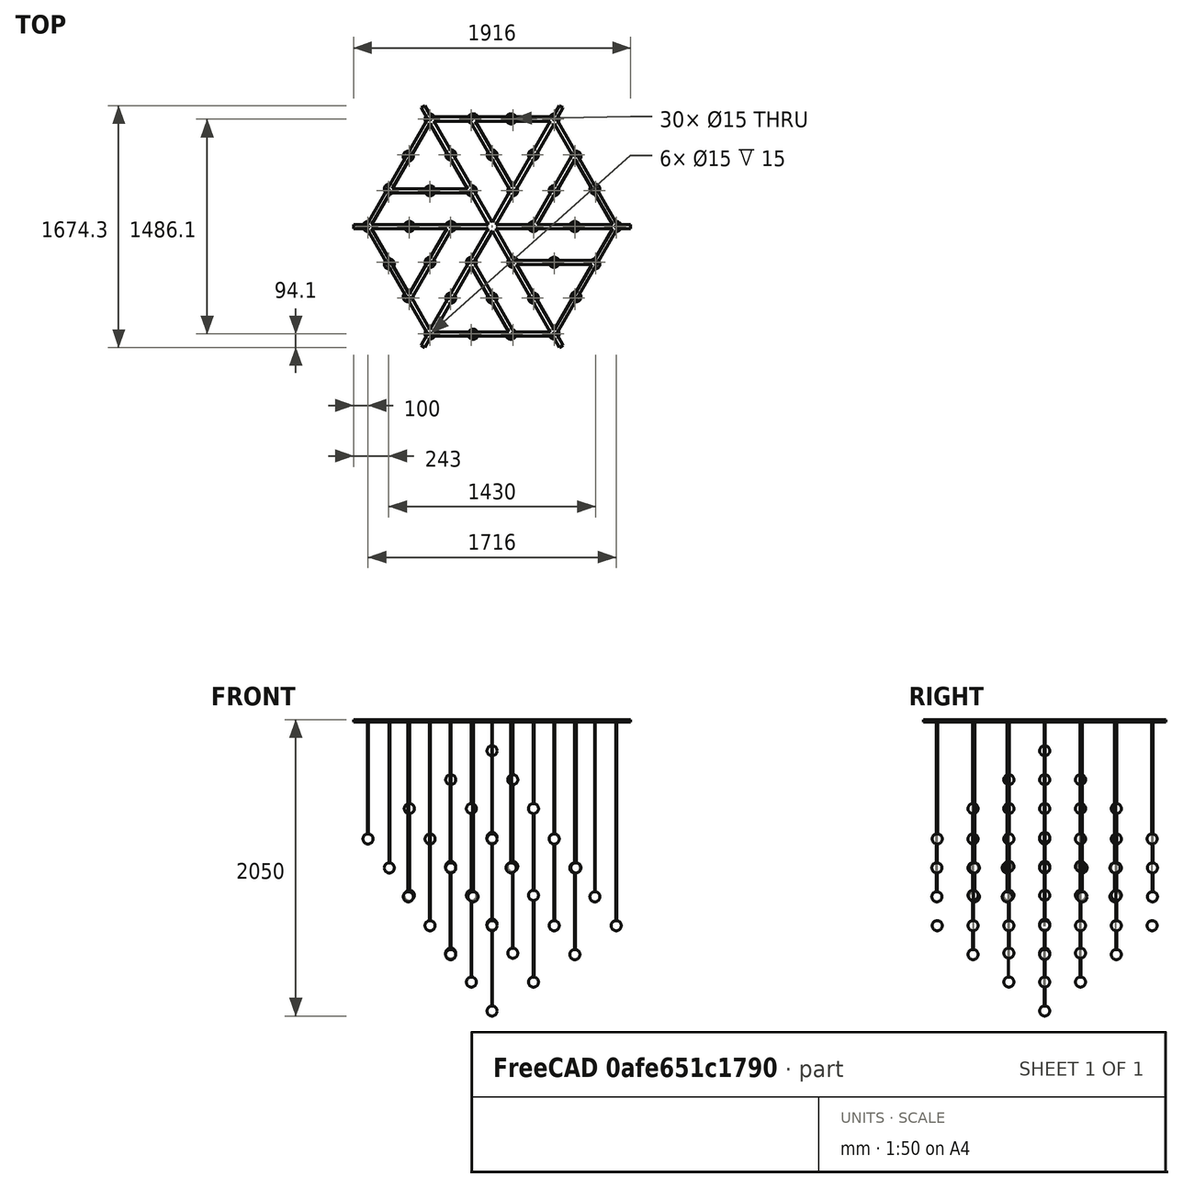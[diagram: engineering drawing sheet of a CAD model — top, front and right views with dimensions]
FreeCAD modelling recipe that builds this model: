
FCSTD DOCUMENT  (FreeCAD 0.19R)
Label: Doc_fabrication
License: Creative Commons Attribution-NonCommercial
LicenseURL: http://creativecommons.org/licenses/by-nc/4.0/
objects: Part::Sphere×64, Part::Fuse×49, Part::Cylinder×37, TechDraw::DrawViewDimension×27, Part::MultiFuse×23, Part::Box×18, TechDraw::DrawSVGTemplate×2, TechDraw::DrawViewPart×2, TechDraw::DrawPage×2, App::DocumentObjectGroup×2, PartDesign::FeatureBase×1, Sketcher::SketchObject×1, PartDesign::Pocket×1, PartDesign::PolarPattern×1, PartDesign::Body×1
note: 197 computed .brp shape members not serialized (recipe doc carries the construction recipe); baked Part::Feature solids carry a one-line shape summary decoded from their .brp

FEATURE [TechDraw::DrawSVGTemplate] Template
  Height = 210
  Orientation = 1
  Width = 297
FEATURE [Part::Cylinder] cylinder
  Angle = 360
  AttacherType = Attacher::AttachEngine3D
  Height = 2000
  Placement = pos=(0,0,-2000) rot=(0,0,1;0rad)
  Radius = 3
FEATURE [Part::Sphere] sphere
  Angle1 = -90
  Angle2 = 90
  Angle3 = 360
  AttacherType = Attacher::AttachEngine3D
  Placement = pos=(0,0,-200) rot=(0,0,1;0rad)
  Radius = 35
FEATURE [Part::Sphere] sphere001
  Angle1 = -90
  Angle2 = 90
  Angle3 = 360
  AttacherType = Attacher::AttachEngine3D
  Placement = pos=(0,0,-800) rot=(0,0,1;0rad)
  Radius = 35
FEATURE [Part::Sphere] sphere002
  Angle1 = -90
  Angle2 = 90
  Angle3 = 360
  AttacherType = Attacher::AttachEngine3D
  Placement = pos=(0,0,-1400) rot=(0,0,1;0rad)
  Radius = 35
FEATURE [Part::Sphere] sphere003
  Angle1 = -90
  Angle2 = 90
  Angle3 = 360
  AttacherType = Attacher::AttachEngine3D
  Placement = pos=(0,0,-2000) rot=(0,0,1;0rad)
  Radius = 35
FEATURE [Part::MultiFuse] Group
  Shapes = -> [sphere,sphere001,sphere002,sphere003]
FEATURE [Part::Fuse] Group001
  Base = -> cylinder
  Tool = -> Group
FEATURE [Part::Cylinder] cylinder001
  Angle = 360
  AttacherType = Attacher::AttachEngine3D
  Height = 1800
  Placement = pos=(0,0,-1800) rot=(0,0,1;0rad)
  Radius = 3
FEATURE [Part::Sphere] sphere004
  Angle1 = -90
  Angle2 = 90
  Angle3 = 360
  AttacherType = Attacher::AttachEngine3D
  Placement = pos=(0,0,-600) rot=(0,0,1;0rad)
  Radius = 35
FEATURE [Part::Sphere] sphere005
  Angle1 = -90
  Angle2 = 90
  Angle3 = 360
  AttacherType = Attacher::AttachEngine3D
  Placement = pos=(0,0,-1200) rot=(0,0,1;0rad)
  Radius = 35
FEATURE [Part::Sphere] sphere006
  Angle1 = -90
  Angle2 = 90
  Angle3 = 360
  AttacherType = Attacher::AttachEngine3D
  Placement = pos=(0,0,-1800) rot=(0,0,1;0rad)
  Radius = 35
FEATURE [Part::MultiFuse] Group002
  Shapes = -> [sphere004,sphere005,sphere006]
FEATURE [Part::Fuse] Group003
  Base = -> cylinder001
  Placement = pos=(286,0,0) rot=(0,0,1;0rad)
  Tool = -> Group002
FEATURE [Part::Cylinder] cylinder002
  Angle = 360
  AttacherType = Attacher::AttachEngine3D
  Height = 1800
  Placement = pos=(0,0,-1800) rot=(0,0,1;0rad)
  Radius = 3
FEATURE [Part::Sphere] sphere007
  Angle1 = -90
  Angle2 = 90
  Angle3 = 360
  AttacherType = Attacher::AttachEngine3D
  Placement = pos=(0,0,-600) rot=(0,0,1;0rad)
  Radius = 35
FEATURE [Part::Sphere] sphere008
  Angle1 = -90
  Angle2 = 90
  Angle3 = 360
  AttacherType = Attacher::AttachEngine3D
  Placement = pos=(0,0,-1200) rot=(0,0,1;0rad)
  Radius = 35
FEATURE [Part::Sphere] sphere009
  Angle1 = -90
  Angle2 = 90
  Angle3 = 360
  AttacherType = Attacher::AttachEngine3D
  Placement = pos=(0,0,-1800) rot=(0,0,1;0rad)
  Radius = 35
FEATURE [Part::MultiFuse] Group004
  Shapes = -> [sphere007,sphere008,sphere009]
FEATURE [Part::Fuse] Group005
  Base = -> cylinder002
  Placement = pos=(-143,247.683,0) rot=(0,0,1;2.0944rad)
  Tool = -> Group004
FEATURE [Part::Cylinder] cylinder003
  Angle = 360
  AttacherType = Attacher::AttachEngine3D
  Height = 1800
  Placement = pos=(0,0,-1800) rot=(0,0,1;0rad)
  Radius = 3
FEATURE [Part::Sphere] sphere010
  Angle1 = -90
  Angle2 = 90
  Angle3 = 360
  AttacherType = Attacher::AttachEngine3D
  Placement = pos=(0,0,-600) rot=(0,0,1;0rad)
  Radius = 35
FEATURE [Part::Sphere] sphere011
  Angle1 = -90
  Angle2 = 90
  Angle3 = 360
  AttacherType = Attacher::AttachEngine3D
  Placement = pos=(0,0,-1200) rot=(0,0,1;0rad)
  Radius = 35
FEATURE [Part::Sphere] sphere012
  Angle1 = -90
  Angle2 = 90
  Angle3 = 360
  AttacherType = Attacher::AttachEngine3D
  Placement = pos=(0,0,-1800) rot=(0,0,1;0rad)
  Radius = 35
FEATURE [Part::MultiFuse] Group006
  Shapes = -> [sphere010,sphere011,sphere012]
FEATURE [Part::Fuse] Group007
  Base = -> cylinder003
  Placement = pos=(-143,-247.683,0) rot=(0,0,1;4.18879rad)
  Tool = -> Group006
FEATURE [Part::MultiFuse] Group008
  Shapes = -> [Group003,Group005,Group007]
FEATURE [Part::Cylinder] cylinder004
  Angle = 360
  AttacherType = Attacher::AttachEngine3D
  Height = 1600
  Placement = pos=(0,0,-1600) rot=(0,0,1;0rad)
  Radius = 3
FEATURE [Part::Sphere] sphere013
  Angle1 = -90
  Angle2 = 90
  Angle3 = 360
  AttacherType = Attacher::AttachEngine3D
  Placement = pos=(0,0,-400) rot=(0,0,1;0rad)
  Radius = 35
FEATURE [Part::Sphere] sphere014
  Angle1 = -90
  Angle2 = 90
  Angle3 = 360
  AttacherType = Attacher::AttachEngine3D
  Placement = pos=(0,0,-1000) rot=(0,0,1;0rad)
  Radius = 35
FEATURE [Part::Sphere] sphere015
  Angle1 = -90
  Angle2 = 90
  Angle3 = 360
  AttacherType = Attacher::AttachEngine3D
  Placement = pos=(0,0,-1600) rot=(0,0,1;0rad)
  Radius = 35
FEATURE [Part::MultiFuse] Group009
  Shapes = -> [sphere013,sphere014,sphere015]
FEATURE [Part::Fuse] Group010
  Base = -> cylinder004
  Placement = pos=(143,247.683,0) rot=(0,0,1;1.0472rad)
  Tool = -> Group009
FEATURE [Part::Cylinder] cylinder005
  Angle = 360
  AttacherType = Attacher::AttachEngine3D
  Height = 1600
  Placement = pos=(0,0,-1600) rot=(0,0,1;0rad)
  Radius = 3
FEATURE [Part::Sphere] sphere016
  Angle1 = -90
  Angle2 = 90
  Angle3 = 360
  AttacherType = Attacher::AttachEngine3D
  Placement = pos=(0,0,-400) rot=(0,0,1;0rad)
  Radius = 35
FEATURE [Part::Sphere] sphere017
  Angle1 = -90
  Angle2 = 90
  Angle3 = 360
  AttacherType = Attacher::AttachEngine3D
  Placement = pos=(0,0,-1000) rot=(0,0,1;0rad)
  Radius = 35
FEATURE [Part::Sphere] sphere018
  Angle1 = -90
  Angle2 = 90
  Angle3 = 360
  AttacherType = Attacher::AttachEngine3D
  Placement = pos=(0,0,-1600) rot=(0,0,1;0rad)
  Radius = 35
FEATURE [Part::MultiFuse] Group011
  Shapes = -> [sphere016,sphere017,sphere018]
FEATURE [Part::Fuse] Group012
  Base = -> cylinder005
  Placement = pos=(-286,3.5e-14,0) rot=(0,0,1;3.14159rad)
  Tool = -> Group011
FEATURE [Part::Cylinder] cylinder006
  Angle = 360
  AttacherType = Attacher::AttachEngine3D
  Height = 1600
  Placement = pos=(0,0,-1600) rot=(0,0,1;0rad)
  Radius = 3
FEATURE [Part::Sphere] sphere019
  Angle1 = -90
  Angle2 = 90
  Angle3 = 360
  AttacherType = Attacher::AttachEngine3D
  Placement = pos=(0,0,-400) rot=(0,0,1;0rad)
  Radius = 35
FEATURE [Part::Sphere] sphere020
  Angle1 = -90
  Angle2 = 90
  Angle3 = 360
  AttacherType = Attacher::AttachEngine3D
  Placement = pos=(0,0,-1000) rot=(0,0,1;0rad)
  Radius = 35
FEATURE [Part::Sphere] sphere021
  Angle1 = -90
  Angle2 = 90
  Angle3 = 360
  AttacherType = Attacher::AttachEngine3D
  Placement = pos=(0,0,-1600) rot=(0,0,1;0rad)
  Radius = 35
FEATURE [Part::MultiFuse] Group013
  Shapes = -> [sphere019,sphere020,sphere021]
FEATURE [Part::Fuse] Group014
  Base = -> cylinder006
  Placement = pos=(143,-247.683,0) rot=(0,0,-1;1.0472rad)
  Tool = -> Group013
FEATURE [Part::MultiFuse] Group015
  Shapes = -> [Group010,Group012,Group014]
FEATURE [Part::Cylinder] cylinder007
  Angle = 360
  AttacherType = Attacher::AttachEngine3D
  Height = 1610
  Placement = pos=(0,0,-1610) rot=(0,0,1;0rad)
  Radius = 3
FEATURE [Part::Sphere] sphere022
  Angle1 = -90
  Angle2 = 90
  Angle3 = 360
  AttacherType = Attacher::AttachEngine3D
  Placement = pos=(0,0,-1010) rot=(0,0,1;0rad)
  Radius = 35
FEATURE [Part::Sphere] sphere023
  Angle1 = -90
  Angle2 = 90
  Angle3 = 360
  AttacherType = Attacher::AttachEngine3D
  Placement = pos=(0,0,-1610) rot=(0,0,1;0rad)
  Radius = 35
FEATURE [Part::Fuse] Group016
  Base = -> sphere022
  Tool = -> sphere023
FEATURE [Part::Fuse] Group017
  Base = -> cylinder007
  Placement = pos=(572,0,0) rot=(0,0,1;0rad)
  Tool = -> Group016
FEATURE [Part::Cylinder] cylinder008
  Angle = 360
  AttacherType = Attacher::AttachEngine3D
  Height = 1610
  Placement = pos=(0,0,-1610) rot=(0,0,1;0rad)
  Radius = 3
FEATURE [Part::Sphere] sphere024
  Angle1 = -90
  Angle2 = 90
  Angle3 = 360
  AttacherType = Attacher::AttachEngine3D
  Placement = pos=(0,0,-1010) rot=(0,0,1;0rad)
  Radius = 35
FEATURE [Part::Sphere] sphere025
  Angle1 = -90
  Angle2 = 90
  Angle3 = 360
  AttacherType = Attacher::AttachEngine3D
  Placement = pos=(0,0,-1610) rot=(0,0,1;0rad)
  Radius = 35
FEATURE [Part::Fuse] Group018
  Base = -> sphere024
  Tool = -> sphere025
FEATURE [Part::Fuse] Group019
  Base = -> cylinder008
  Placement = pos=(-286,495.367,0) rot=(0,0,1;2.0944rad)
  Tool = -> Group018
FEATURE [Part::Cylinder] cylinder009
  Angle = 360
  AttacherType = Attacher::AttachEngine3D
  Height = 1610
  Placement = pos=(0,0,-1610) rot=(0,0,1;0rad)
  Radius = 3
FEATURE [Part::Sphere] sphere026
  Angle1 = -90
  Angle2 = 90
  Angle3 = 360
  AttacherType = Attacher::AttachEngine3D
  Placement = pos=(0,0,-1010) rot=(0,0,1;0rad)
  Radius = 35
FEATURE [Part::Sphere] sphere027
  Angle1 = -90
  Angle2 = 90
  Angle3 = 360
  AttacherType = Attacher::AttachEngine3D
  Placement = pos=(0,0,-1610) rot=(0,0,1;0rad)
  Radius = 35
FEATURE [Part::Fuse] Group020
  Base = -> sphere026
  Tool = -> sphere027
FEATURE [Part::Fuse] Group021
  Base = -> cylinder009
  Placement = pos=(-286,-495.367,0) rot=(0,0,1;4.18879rad)
  Tool = -> Group020
FEATURE [Part::MultiFuse] Group022
  Shapes = -> [Group017,Group019,Group021]
FEATURE [Part::Cylinder] cylinder010
  Angle = 360
  AttacherType = Attacher::AttachEngine3D
  Height = 1200
  Placement = pos=(0,0,-1200) rot=(0,0,1;0rad)
  Radius = 3
FEATURE [Part::Sphere] sphere028
  Angle1 = -90
  Angle2 = 90
  Angle3 = 360
  AttacherType = Attacher::AttachEngine3D
  Placement = pos=(0,0,-600) rot=(0,0,1;0rad)
  Radius = 35
FEATURE [Part::Sphere] sphere029
  Angle1 = -90
  Angle2 = 90
  Angle3 = 360
  AttacherType = Attacher::AttachEngine3D
  Placement = pos=(0,0,-1200) rot=(0,0,1;0rad)
  Radius = 35
FEATURE [Part::Fuse] Group023
  Base = -> sphere028
  Tool = -> sphere029
FEATURE [Part::Fuse] Group024
  Base = -> cylinder010
  Placement = pos=(286,495.367,0) rot=(0,0,1;1.0472rad)
  Tool = -> Group023
FEATURE [Part::Cylinder] cylinder011
  Angle = 360
  AttacherType = Attacher::AttachEngine3D
  Height = 1200
  Placement = pos=(0,0,-1200) rot=(0,0,1;0rad)
  Radius = 3
FEATURE [Part::Sphere] sphere030
  Angle1 = -90
  Angle2 = 90
  Angle3 = 360
  AttacherType = Attacher::AttachEngine3D
  Placement = pos=(0,0,-600) rot=(0,0,1;0rad)
  Radius = 35
FEATURE [Part::Sphere] sphere031
  Angle1 = -90
  Angle2 = 90
  Angle3 = 360
  AttacherType = Attacher::AttachEngine3D
  Placement = pos=(0,0,-1200) rot=(0,0,1;0rad)
  Radius = 35
FEATURE [Part::Fuse] Group025
  Base = -> sphere030
  Tool = -> sphere031
FEATURE [Part::Fuse] Group026
  Base = -> cylinder011
  Placement = pos=(-572,7e-14,0) rot=(0,0,1;3.14159rad)
  Tool = -> Group025
FEATURE [Part::Cylinder] cylinder012
  Angle = 360
  AttacherType = Attacher::AttachEngine3D
  Height = 1200
  Placement = pos=(0,0,-1200) rot=(0,0,1;0rad)
  Radius = 3
FEATURE [Part::Sphere] sphere032
  Angle1 = -90
  Angle2 = 90
  Angle3 = 360
  AttacherType = Attacher::AttachEngine3D
  Placement = pos=(0,0,-600) rot=(0,0,1;0rad)
  Radius = 35
FEATURE [Part::Sphere] sphere033
  Angle1 = -90
  Angle2 = 90
  Angle3 = 360
  AttacherType = Attacher::AttachEngine3D
  Placement = pos=(0,0,-1200) rot=(0,0,1;0rad)
  Radius = 35
FEATURE [Part::Fuse] Group027
  Base = -> sphere032
  Tool = -> sphere033
FEATURE [Part::Fuse] Group028
  Base = -> cylinder012
  Placement = pos=(286,-495.367,0) rot=(0,0,-1;1.0472rad)
  Tool = -> Group027
FEATURE [Part::MultiFuse] Group029
  Shapes = -> [Group024,Group026,Group028]
FEATURE [Part::Cylinder] cylinder013
  Angle = 360
  AttacherType = Attacher::AttachEngine3D
  Height = 1410
  Placement = pos=(0,0,-1410) rot=(0,0,1;0rad)
  Radius = 3
FEATURE [Part::Box] cube
  AttacherType = Attacher::AttachEngine3D
  Height = 15
  Length = 958
  Placement = pos=(0,-15,0) rot=(0,0,1;0rad)
  Width = 30
FEATURE [Part::Sphere] sphere034
  Angle1 = -90
  Angle2 = 90
  Angle3 = 360
  AttacherType = Attacher::AttachEngine3D
  Placement = pos=(0,0,-810) rot=(0,0,1;0rad)
  Radius = 35
FEATURE [Part::Sphere] sphere035
  Angle1 = -90
  Angle2 = 90
  Angle3 = 360
  AttacherType = Attacher::AttachEngine3D
  Placement = pos=(0,0,-1410) rot=(0,0,1;0rad)
  Radius = 35
FEATURE [Part::Fuse] Group030
  Base = -> sphere034
  Tool = -> sphere035
FEATURE [Part::Fuse] Group031
  Base = -> cylinder013
  Placement = pos=(429,247.683,0) rot=(0,0,1;0.523599rad)
  Tool = -> Group030
FEATURE [Part::Cylinder] cylinder014
  Angle = 360
  AttacherType = Attacher::AttachEngine3D
  Height = 1410
  Placement = pos=(0,0,-1410) rot=(0,0,1;0rad)
  Radius = 3
FEATURE [Part::Sphere] sphere036
  Angle1 = -90
  Angle2 = 90
  Angle3 = 360
  AttacherType = Attacher::AttachEngine3D
  Placement = pos=(0,0,-810) rot=(0,0,1;0rad)
  Radius = 35
FEATURE [Part::Sphere] sphere037
  Angle1 = -90
  Angle2 = 90
  Angle3 = 360
  AttacherType = Attacher::AttachEngine3D
  Placement = pos=(0,0,-1410) rot=(0,0,1;0rad)
  Radius = 35
FEATURE [Part::Fuse] Group032
  Base = -> sphere036
  Tool = -> sphere037
FEATURE [Part::Fuse] Group033
  Base = -> cylinder014
  Placement = pos=(1.1e-13,495.367,0) rot=(0,0,1;1.5708rad)
  Tool = -> Group032
FEATURE [Part::Cylinder] cylinder015
  Angle = 360
  AttacherType = Attacher::AttachEngine3D
  Height = 1410
  Placement = pos=(0,0,-1410) rot=(0,0,1;0rad)
  Radius = 3
FEATURE [Part::Sphere] sphere038
  Angle1 = -90
  Angle2 = 90
  Angle3 = 360
  AttacherType = Attacher::AttachEngine3D
  Placement = pos=(0,0,-810) rot=(0,0,1;0rad)
  Radius = 35
FEATURE [Part::Sphere] sphere039
  Angle1 = -90
  Angle2 = 90
  Angle3 = 360
  AttacherType = Attacher::AttachEngine3D
  Placement = pos=(0,0,-1410) rot=(0,0,1;0rad)
  Radius = 35
FEATURE [Part::Fuse] Group034
  Base = -> sphere038
  Tool = -> sphere039
FEATURE [Part::Fuse] Group035
  Base = -> cylinder015
  Placement = pos=(-429,247.683,0) rot=(0,0,1;2.61799rad)
  Tool = -> Group034
FEATURE [Part::Cylinder] cylinder016
  Angle = 360
  AttacherType = Attacher::AttachEngine3D
  Height = 1410
  Placement = pos=(0,0,-1410) rot=(0,0,1;0rad)
  Radius = 3
FEATURE [Part::Sphere] sphere040
  Angle1 = -90
  Angle2 = 90
  Angle3 = 360
  AttacherType = Attacher::AttachEngine3D
  Placement = pos=(0,0,-810) rot=(0,0,1;0rad)
  Radius = 35
FEATURE [Part::Sphere] sphere041
  Angle1 = -90
  Angle2 = 90
  Angle3 = 360
  AttacherType = Attacher::AttachEngine3D
  Placement = pos=(0,0,-1410) rot=(0,0,1;0rad)
  Radius = 35
FEATURE [Part::Fuse] Group036
  Base = -> sphere040
  Tool = -> sphere041
FEATURE [Part::Fuse] Group037
  Base = -> cylinder016
  Placement = pos=(-429,-247.683,0) rot=(0,0,1;3.66519rad)
  Tool = -> Group036
FEATURE [Part::Cylinder] cylinder017
  Angle = 360
  AttacherType = Attacher::AttachEngine3D
  Height = 1410
  Placement = pos=(0,0,-1410) rot=(0,0,1;0rad)
  Radius = 3
FEATURE [Part::Sphere] sphere042
  Angle1 = -90
  Angle2 = 90
  Angle3 = 360
  AttacherType = Attacher::AttachEngine3D
  Placement = pos=(0,0,-810) rot=(0,0,1;0rad)
  Radius = 35
FEATURE [Part::Sphere] sphere043
  Angle1 = -90
  Angle2 = 90
  Angle3 = 360
  AttacherType = Attacher::AttachEngine3D
  Placement = pos=(0,0,-1410) rot=(0,0,1;0rad)
  Radius = 35
FEATURE [Part::Fuse] Group038
  Base = -> sphere042
  Tool = -> sphere043
FEATURE [Part::Fuse] Group039
  Base = -> cylinder017
  Placement = pos=(1.1e-13,-495.367,0) rot=(0,0,-1;1.5708rad)
  Tool = -> Group038
FEATURE [Part::Cylinder] cylinder018
  Angle = 360
  AttacherType = Attacher::AttachEngine3D
  Height = 1410
  Placement = pos=(0,0,-1410) rot=(0,0,1;0rad)
  Radius = 3
FEATURE [Part::Sphere] sphere044
  Angle1 = -90
  Angle2 = 90
  Angle3 = 360
  AttacherType = Attacher::AttachEngine3D
  Placement = pos=(0,0,-810) rot=(0,0,1;0rad)
  Radius = 35
FEATURE [Part::Sphere] sphere045
  Angle1 = -90
  Angle2 = 90
  Angle3 = 360
  AttacherType = Attacher::AttachEngine3D
  Placement = pos=(0,0,-1410) rot=(0,0,1;0rad)
  Radius = 35
FEATURE [Part::Fuse] Group040
  Base = -> sphere044
  Tool = -> sphere045
FEATURE [Part::Fuse] Group041
  Base = -> cylinder018
  Placement = pos=(429,-247.683,0) rot=(0,0,-1;0.523599rad)
  Tool = -> Group040
FEATURE [Part::MultiFuse] Group042
  Shapes = -> [Group031,Group033,Group035,Group037,Group039,Group041]
FEATURE [Part::Cylinder] cylinder019
  Angle = 360
  AttacherType = Attacher::AttachEngine3D
  Height = 1410
  Placement = pos=(0,0,-1410) rot=(0,0,1;0rad)
  Radius = 3
FEATURE [Part::Sphere] sphere046
  Angle1 = -90
  Angle2 = 90
  Angle3 = 360
  AttacherType = Attacher::AttachEngine3D
  Placement = pos=(0,0,-1410) rot=(0,0,1;0rad)
  Radius = 35
FEATURE [Part::Fuse] Group043
  Base = -> cylinder019
  Placement = pos=(858,0,0) rot=(0,0,1;0rad)
  Tool = -> sphere046
FEATURE [Part::Cylinder] cylinder020
  Angle = 360
  AttacherType = Attacher::AttachEngine3D
  Height = 1210
  Placement = pos=(0,0,-1210) rot=(0,0,1;0rad)
  Radius = 3
FEATURE [Part::Sphere] sphere047
  Angle1 = -90
  Angle2 = 90
  Angle3 = 360
  AttacherType = Attacher::AttachEngine3D
  Placement = pos=(0,0,-1210) rot=(0,0,1;0rad)
  Radius = 35
FEATURE [Part::Fuse] Group044
  Base = -> cylinder020
  Placement = pos=(711.051,258.802,0) rot=(0,0,1;0.349066rad)
  Tool = -> sphere047
FEATURE [Part::Cylinder] cylinder021
  Angle = 360
  AttacherType = Attacher::AttachEngine3D
  Height = 1010
  Placement = pos=(0,0,-1010) rot=(0,0,1;0rad)
  Radius = 3
FEATURE [Part::Sphere] sphere048
  Angle1 = -90
  Angle2 = 90
  Angle3 = 360
  AttacherType = Attacher::AttachEngine3D
  Placement = pos=(0,0,-1010) rot=(0,0,1;0rad)
  Radius = 35
FEATURE [Part::Fuse] Group045
  Base = -> cylinder021
  Placement = pos=(579.654,486.388,0) rot=(0,0,1;0.698132rad)
  Tool = -> sphere048
FEATURE [Part::Cylinder] cylinder022
  Angle = 360
  AttacherType = Attacher::AttachEngine3D
  Height = 810
  Placement = pos=(0,0,-810) rot=(0,0,1;0rad)
  Radius = 3
FEATURE [Part::Sphere] sphere049
  Angle1 = -90
  Angle2 = 90
  Angle3 = 360
  AttacherType = Attacher::AttachEngine3D
  Placement = pos=(0,0,-810) rot=(0,0,1;0rad)
  Radius = 35
FEATURE [Part::Fuse] Group046
  Base = -> cylinder022
  Placement = pos=(429,743.05,0) rot=(0,0,1;1.0472rad)
  Tool = -> sphere049
FEATURE [Part::Cylinder] cylinder023
  Angle = 360
  AttacherType = Attacher::AttachEngine3D
  Height = 1010
  Placement = pos=(0,0,-1010) rot=(0,0,1;0rad)
  Radius = 3
FEATURE [Part::Sphere] sphere050
  Angle1 = -90
  Angle2 = 90
  Angle3 = 360
  AttacherType = Attacher::AttachEngine3D
  Placement = pos=(0,0,-1010) rot=(0,0,1;0rad)
  Radius = 35
FEATURE [Part::Fuse] Group047
  Base = -> cylinder023
  Placement = pos=(131.397,745.189,0) rot=(0,0,1;1.39626rad)
  Tool = -> sphere050
FEATURE [Part::Cylinder] cylinder024
  Angle = 360
  AttacherType = Attacher::AttachEngine3D
  Height = 1210
  Placement = pos=(0,0,-1210) rot=(0,0,1;0rad)
  Radius = 3
FEATURE [Part::Sphere] sphere051
  Angle1 = -90
  Angle2 = 90
  Angle3 = 360
  AttacherType = Attacher::AttachEngine3D
  Placement = pos=(0,0,-1210) rot=(0,0,1;0rad)
  Radius = 35
FEATURE [Part::Fuse] Group048
  Base = -> cylinder024
  Placement = pos=(-131.397,745.189,0) rot=(0,0,1;1.74533rad)
  Tool = -> sphere051
FEATURE [Part::MultiFuse] Group049
  Shapes = -> [Group043,Group044,Group045,Group046,Group047,Group048]
FEATURE [Part::Cylinder] cylinder025
  Angle = 360
  AttacherType = Attacher::AttachEngine3D
  Height = 1410
  Placement = pos=(0,0,-1410) rot=(0,0,1;0rad)
  Radius = 3
FEATURE [Part::Sphere] sphere052
  Angle1 = -90
  Angle2 = 90
  Angle3 = 360
  AttacherType = Attacher::AttachEngine3D
  Placement = pos=(0,0,-1410) rot=(0,0,1;0rad)
  Radius = 35
FEATURE [Part::Fuse] Group050
  Base = -> cylinder025
  Placement = pos=(-429,743.05,0) rot=(0,0,1;2.0944rad)
  Tool = -> sphere052
FEATURE [Part::Cylinder] cylinder026
  Angle = 360
  AttacherType = Attacher::AttachEngine3D
  Height = 1210
  Placement = pos=(0,0,-1210) rot=(0,0,1;0rad)
  Radius = 3
FEATURE [Part::Sphere] sphere053
  Angle1 = -90
  Angle2 = 90
  Angle3 = 360
  AttacherType = Attacher::AttachEngine3D
  Placement = pos=(0,0,-1210) rot=(0,0,1;0rad)
  Radius = 35
FEATURE [Part::Fuse] Group051
  Base = -> cylinder026
  Placement = pos=(-579.654,486.388,0) rot=(0,0,1;2.44346rad)
  Tool = -> sphere053
FEATURE [Part::Cylinder] cylinder027
  Angle = 360
  AttacherType = Attacher::AttachEngine3D
  Height = 1010
  Placement = pos=(0,0,-1010) rot=(0,0,1;0rad)
  Radius = 3
FEATURE [Part::Sphere] sphere054
  Angle1 = -90
  Angle2 = 90
  Angle3 = 360
  AttacherType = Attacher::AttachEngine3D
  Placement = pos=(0,0,-1010) rot=(0,0,1;0rad)
  Radius = 35
FEATURE [Part::Fuse] Group052
  Base = -> cylinder027
  Placement = pos=(-711.051,258.802,0) rot=(0,0,1;2.79253rad)
  Tool = -> sphere054
FEATURE [Part::Cylinder] cylinder028
  Angle = 360
  AttacherType = Attacher::AttachEngine3D
  Height = 810
  Placement = pos=(0,0,-810) rot=(0,0,1;0rad)
  Radius = 3
FEATURE [Part::Sphere] sphere055
  Angle1 = -90
  Angle2 = 90
  Angle3 = 360
  AttacherType = Attacher::AttachEngine3D
  Placement = pos=(0,0,-810) rot=(0,0,1;0rad)
  Radius = 35
FEATURE [Part::Fuse] Group053
  Base = -> cylinder028
  Placement = pos=(-858,1.05e-13,0) rot=(0,0,1;3.14159rad)
  Tool = -> sphere055
FEATURE [Part::Cylinder] cylinder029
  Angle = 360
  AttacherType = Attacher::AttachEngine3D
  Height = 1010
  Placement = pos=(0,0,-1010) rot=(0,0,1;0rad)
  Radius = 3
FEATURE [Part::Sphere] sphere056
  Angle1 = -90
  Angle2 = 90
  Angle3 = 360
  AttacherType = Attacher::AttachEngine3D
  Placement = pos=(0,0,-1010) rot=(0,0,1;0rad)
  Radius = 35
FEATURE [Part::Fuse] Group054
  Base = -> cylinder029
  Placement = pos=(-711.051,-258.802,0) rot=(0,0,1;3.49066rad)
  Tool = -> sphere056
FEATURE [Part::Cylinder] cylinder030
  Angle = 360
  AttacherType = Attacher::AttachEngine3D
  Height = 1210
  Placement = pos=(0,0,-1210) rot=(0,0,1;0rad)
  Radius = 3
FEATURE [Part::Sphere] sphere057
  Angle1 = -90
  Angle2 = 90
  Angle3 = 360
  AttacherType = Attacher::AttachEngine3D
  Placement = pos=(0,0,-1210) rot=(0,0,1;0rad)
  Radius = 35
FEATURE [Part::Fuse] Group055
  Base = -> cylinder030
  Placement = pos=(-579.654,-486.388,0) rot=(0,0,1;3.83972rad)
  Tool = -> sphere057
FEATURE [Part::MultiFuse] Group056
  Shapes = -> [Group050,Group051,Group052,Group053,Group054,Group055]
FEATURE [Part::Cylinder] cylinder031
  Angle = 360
  AttacherType = Attacher::AttachEngine3D
  Height = 1410
  Placement = pos=(0,0,-1410) rot=(0,0,1;0rad)
  Radius = 3
FEATURE [Part::Sphere] sphere058
  Angle1 = -90
  Angle2 = 90
  Angle3 = 360
  AttacherType = Attacher::AttachEngine3D
  Placement = pos=(0,0,-1410) rot=(0,0,1;0rad)
  Radius = 35
FEATURE [Part::Fuse] Group057
  Base = -> cylinder031
  Placement = pos=(-429,-743.05,0) rot=(0,0,1;4.18879rad)
  Tool = -> sphere058
FEATURE [Part::Cylinder] cylinder032
  Angle = 360
  AttacherType = Attacher::AttachEngine3D
  Height = 1210
  Placement = pos=(0,0,-1210) rot=(0,0,1;0rad)
  Radius = 3
FEATURE [Part::Sphere] sphere059
  Angle1 = -90
  Angle2 = 90
  Angle3 = 360
  AttacherType = Attacher::AttachEngine3D
  Placement = pos=(0,0,-1210) rot=(0,0,1;0rad)
  Radius = 35
FEATURE [Part::Fuse] Group058
  Base = -> cylinder032
  Placement = pos=(-131.397,-745.189,0) rot=(0,0,-1;1.74533rad)
  Tool = -> sphere059
FEATURE [Part::Cylinder] cylinder033
  Angle = 360
  AttacherType = Attacher::AttachEngine3D
  Height = 1010
  Placement = pos=(0,0,-1010) rot=(0,0,1;0rad)
  Radius = 3
FEATURE [Part::Sphere] sphere060
  Angle1 = -90
  Angle2 = 90
  Angle3 = 360
  AttacherType = Attacher::AttachEngine3D
  Placement = pos=(0,0,-1010) rot=(0,0,1;0rad)
  Radius = 35
FEATURE [Part::Fuse] Group059
  Base = -> cylinder033
  Placement = pos=(131.397,-745.189,0) rot=(0,0,-1;1.39626rad)
  Tool = -> sphere060
FEATURE [Part::Cylinder] cylinder034
  Angle = 360
  AttacherType = Attacher::AttachEngine3D
  Height = 810
  Placement = pos=(0,0,-810) rot=(0,0,1;0rad)
  Radius = 3
FEATURE [Part::Sphere] sphere061
  Angle1 = -90
  Angle2 = 90
  Angle3 = 360
  AttacherType = Attacher::AttachEngine3D
  Placement = pos=(0,0,-810) rot=(0,0,1;0rad)
  Radius = 35
FEATURE [Part::Fuse] Group060
  Base = -> cylinder034
  Placement = pos=(429,-743.05,0) rot=(0,0,-1;1.0472rad)
  Tool = -> sphere061
FEATURE [Part::Cylinder] cylinder035
  Angle = 360
  AttacherType = Attacher::AttachEngine3D
  Height = 1010
  Placement = pos=(0,0,-1010) rot=(0,0,1;0rad)
  Radius = 3
FEATURE [Part::Sphere] sphere062
  Angle1 = -90
  Angle2 = 90
  Angle3 = 360
  AttacherType = Attacher::AttachEngine3D
  Placement = pos=(0,0,-1010) rot=(0,0,1;0rad)
  Radius = 35
FEATURE [Part::Fuse] Group061
  Base = -> cylinder035
  Placement = pos=(579.654,-486.388,0) rot=(0,0,-1;0.698132rad)
  Tool = -> sphere062
FEATURE [Part::Cylinder] cylinder036
  Angle = 360
  AttacherType = Attacher::AttachEngine3D
  Height = 1210
  Placement = pos=(0,0,-1210) rot=(0,0,1;0rad)
  Radius = 3
FEATURE [Part::Sphere] sphere063
  Angle1 = -90
  Angle2 = 90
  Angle3 = 360
  AttacherType = Attacher::AttachEngine3D
  Placement = pos=(0,0,-1210) rot=(0,0,1;0rad)
  Radius = 35
FEATURE [Part::Fuse] Group062
  Base = -> cylinder036
  Placement = pos=(711.051,-258.802,0) rot=(0,0,-1;0.349066rad)
  Tool = -> sphere063
FEATURE [Part::MultiFuse] Group063
  Shapes = -> [Group057,Group058,Group059,Group060,Group061,Group062]
FEATURE [Part::MultiFuse] Group064
  Shapes = -> [Group049,Group056,Group063]
FEATURE [Part::Box] cube001
  AttacherType = Attacher::AttachEngine3D
  Height = 15
  Length = 858
  Placement = pos=(870.99,7.5,0) rot=(0,0,1;2.0944rad)
  Width = 30
FEATURE [Part::Box] cube002
  AttacherType = Attacher::AttachEngine3D
  Height = 15
  Length = 572
  Placement = pos=(298.99,-7.5,0) rot=(0,0,1;1.0472rad)
  Width = 30
FEATURE [Part::MultiFuse] Group065
  Shapes = -> [cube,cube001,cube002]
FEATURE [Part::Box] cube003
  AttacherType = Attacher::AttachEngine3D
  Height = 15
  Length = 958
  Placement = pos=(0,-15,0) rot=(0,0,1;0rad)
  Width = 30
FEATURE [Part::Box] cube004
  AttacherType = Attacher::AttachEngine3D
  Height = 15
  Length = 858
  Placement = pos=(870.99,7.5,0) rot=(0,0,1;2.0944rad)
  Width = 30
FEATURE [Part::Box] cube005
  AttacherType = Attacher::AttachEngine3D
  Height = 15
  Length = 572
  Placement = pos=(298.99,-7.5,0) rot=(0,0,1;1.0472rad)
  Width = 30
FEATURE [Part::MultiFuse] Group066
  Placement = pos=(0,0,0) rot=(0,0,1;1.0472rad)
  Shapes = -> [cube003,cube004,cube005]
FEATURE [Part::Box] cube006
  AttacherType = Attacher::AttachEngine3D
  Height = 15
  Length = 958
  Placement = pos=(0,-15,0) rot=(0,0,1;0rad)
  Width = 30
FEATURE [Part::Box] cube007
  AttacherType = Attacher::AttachEngine3D
  Height = 15
  Length = 858
  Placement = pos=(870.99,7.5,0) rot=(0,0,1;2.0944rad)
  Width = 30
FEATURE [Part::Box] cube008
  AttacherType = Attacher::AttachEngine3D
  Height = 15
  Length = 572
  Placement = pos=(298.99,-7.5,0) rot=(0,0,1;1.0472rad)
  Width = 30
FEATURE [Part::MultiFuse] Group067
  Placement = pos=(0,0,0) rot=(0,0,1;2.0944rad)
  Shapes = -> [cube006,cube007,cube008]
FEATURE [Part::Box] cube009
  AttacherType = Attacher::AttachEngine3D
  Height = 15
  Length = 958
  Placement = pos=(0,-15,0) rot=(0,0,1;0rad)
  Width = 30
FEATURE [Part::Box] cube010
  AttacherType = Attacher::AttachEngine3D
  Height = 15
  Length = 858
  Placement = pos=(870.99,7.5,0) rot=(0,0,1;2.0944rad)
  Width = 30
FEATURE [Part::Box] cube011
  AttacherType = Attacher::AttachEngine3D
  Height = 15
  Length = 572
  Placement = pos=(298.99,-7.5,0) rot=(0,0,1;1.0472rad)
  Width = 30
FEATURE [Part::MultiFuse] Group068
  Placement = pos=(0,0,0) rot=(0,0,1;3.14159rad)
  Shapes = -> [cube009,cube010,cube011]
FEATURE [Part::Box] cube012
  AttacherType = Attacher::AttachEngine3D
  Height = 15
  Length = 958
  Placement = pos=(0,-15,0) rot=(0,0,1;0rad)
  Width = 30
FEATURE [Part::Box] cube013
  AttacherType = Attacher::AttachEngine3D
  Height = 15
  Length = 858
  Placement = pos=(870.99,7.5,0) rot=(0,0,1;2.0944rad)
  Width = 30
FEATURE [Part::Box] cube014
  AttacherType = Attacher::AttachEngine3D
  Height = 15
  Length = 572
  Placement = pos=(298.99,-7.5,0) rot=(0,0,1;1.0472rad)
  Width = 30
FEATURE [Part::MultiFuse] Group069
  Placement = pos=(0,0,0) rot=(0,0,1;4.18879rad)
  Shapes = -> [cube012,cube013,cube014]
FEATURE [Part::Box] cube015
  AttacherType = Attacher::AttachEngine3D
  Height = 15
  Length = 958
  Placement = pos=(0,-15,0) rot=(0,0,1;0rad)
  Width = 30
FEATURE [Part::Box] cube016
  AttacherType = Attacher::AttachEngine3D
  Height = 15
  Length = 858
  Placement = pos=(870.99,7.5,0) rot=(0,0,1;2.0944rad)
  Width = 30
FEATURE [Part::Box] cube017
  AttacherType = Attacher::AttachEngine3D
  Height = 15
  Length = 572
  Placement = pos=(298.99,-7.5,0) rot=(0,0,1;1.0472rad)
  Width = 30
FEATURE [Part::MultiFuse] Group070
  Placement = pos=(0,0,0) rot=(0,0,-1;1.0472rad)
  Shapes = -> [cube015,cube016,cube017]
FEATURE [Part::MultiFuse] Group071  label="support"
  Shapes = -> [Group065,Group066,Group067,Group068,Group069,Group070]
FEATURE [TechDraw::DrawViewPart] View
  CoarseView = false
  Direction = (0,0,1)
  Focus = 100
  HardHidden = false
  IsoCount = 0
  IsoHidden = false
  IsoVisible = false
  LockPosition = false
  Perspective = false
  Rotation = 0
  Scale = 0.1
  ScaleType = 2
  SeamHidden = false
  SeamVisible = true
  SmoothHidden = false
  SmoothVisible = true
  Source = -> [Group071]
  X = 146.8
  XDirection = (1,0,0)
  Y = 107.431
FEATURE [TechDraw::DrawViewDimension] Dimension
  Arbitrary = false
  ArbitraryTolerances = false
  EqualTolerance = true
  FormatSpec = %.2f
  FormatSpecOverTolerance = %+.2f
  FormatSpecUnderTolerance = %+.2f
  Inverted = false
  LockPosition = false
  MeasureType = 1
  OverTolerance = 0
  References2D = -> [View]
  Rotation = 0
  ScaleType = 0
  TheoreticalExact = false
  Type = 1
  UnderTolerance = 0
  X = 42.3238
  Y = -15.6122
FEATURE [TechDraw::DrawViewDimension] Dimension003
  Arbitrary = false
  ArbitraryTolerances = false
  EqualTolerance = true
  FormatSpec = %.2f
  FormatSpecOverTolerance = %+.2f
  FormatSpecUnderTolerance = %+.2f
  Inverted = false
  LockPosition = false
  MeasureType = 1
  OverTolerance = 0
  References2D = -> [View]
  Rotation = 0
  ScaleType = 0
  TheoreticalExact = false
  Type = 1
  UnderTolerance = 0
  X = -48.7713
  Y = 15.9098
FEATURE [TechDraw::DrawViewDimension] Dimension005
  Arbitrary = false
  ArbitraryTolerances = false
  EqualTolerance = true
  FormatSpec = %.2f
  FormatSpecOverTolerance = %+.2f
  FormatSpecUnderTolerance = %+.2f
  Inverted = false
  LockPosition = false
  MeasureType = 1
  OverTolerance = 0
  References2D = -> [View]
  Rotation = 0
  ScaleType = 0
  TheoreticalExact = false
  Type = 6
  UnderTolerance = 0
  X = 55.6746
  Y = 19.6529
FEATURE [TechDraw::DrawViewDimension] Dimension006
  Arbitrary = false
  ArbitraryTolerances = false
  EqualTolerance = true
  FormatSpec = %.2f
  FormatSpecOverTolerance = %+.2f
  FormatSpecUnderTolerance = %+.2f
  Inverted = false
  LockPosition = false
  MeasureType = 1
  OverTolerance = 0
  References2D = -> [View]
  Rotation = 0
  ScaleType = 0
  TheoreticalExact = false
  Type = 0
  UnderTolerance = 0
  X = 80.0015
  Y = 47.5748
FEATURE [TechDraw::DrawViewDimension] Dimension007
  Arbitrary = false
  ArbitraryTolerances = false
  EqualTolerance = true
  FormatSpec = %.2f
  FormatSpecOverTolerance = %+.2f
  FormatSpecUnderTolerance = %+.2f
  Inverted = false
  LockPosition = false
  MeasureType = 1
  OverTolerance = 0
  References2D = -> [View]
  Rotation = 0
  ScaleType = 0
  TheoreticalExact = false
  Type = 0
  UnderTolerance = 0
  X = 78.4692
  Y = 33.3786
FEATURE [TechDraw::DrawViewDimension] Dimension008
  Arbitrary = false
  ArbitraryTolerances = false
  EqualTolerance = true
  FormatSpec = %.2f
  FormatSpecOverTolerance = %+.2f
  FormatSpecUnderTolerance = %+.2f
  Inverted = false
  LockPosition = false
  MeasureType = 1
  OverTolerance = 0
  References2D = -> [View]
  Rotation = 0
  ScaleType = 0
  TheoreticalExact = false
  Type = 1
  UnderTolerance = 0
  X = 41.964
  Y = -9.57634
FEATURE [TechDraw::DrawViewDimension] Dimension009
  Arbitrary = false
  ArbitraryTolerances = false
  EqualTolerance = true
  FormatSpec = %.2f
  FormatSpecOverTolerance = %+.2f
  FormatSpecUnderTolerance = %+.2f
  Inverted = false
  LockPosition = false
  MeasureType = 1
  OverTolerance = 0
  References2D = -> [View]
  Rotation = 0
  ScaleType = 0
  TheoreticalExact = false
  Type = 0
  UnderTolerance = 0
  X = 31.3046
  Y = 34.0986
FEATURE [TechDraw::DrawViewDimension] Dimension010
  Arbitrary = false
  ArbitraryTolerances = false
  EqualTolerance = true
  FormatSpec = %.2f
  FormatSpecOverTolerance = %+.2f
  FormatSpecUnderTolerance = %+.2f
  Inverted = false
  LockPosition = false
  MeasureType = 1
  OverTolerance = 0
  References2D = -> [View]
  Rotation = 0
  ScaleType = 0
  TheoreticalExact = false
  Type = 1
  UnderTolerance = 0
  X = 19.2221
  Y = -4.42818
FEATURE [TechDraw::DrawViewDimension] Dimension011
  Arbitrary = false
  ArbitraryTolerances = false
  EqualTolerance = true
  FormatSpec = %.2f
  FormatSpecOverTolerance = %+.2f
  FormatSpecUnderTolerance = %+.2f
  Inverted = false
  LockPosition = false
  MeasureType = 1
  OverTolerance = 0
  References2D = -> [View]
  Rotation = 0
  ScaleType = 0
  TheoreticalExact = false
  Type = 0
  UnderTolerance = 0
  X = 36.8327
  Y = 87.4938
FEATURE [TechDraw::DrawViewDimension] Dimension012
  Arbitrary = false
  ArbitraryTolerances = false
  EqualTolerance = true
  FormatSpec = %.2f
  FormatSpecOverTolerance = %+.2f
  FormatSpecUnderTolerance = %+.2f
  Inverted = false
  LockPosition = false
  MeasureType = 1
  OverTolerance = 0
  References2D = -> [View]
  Rotation = 0
  ScaleType = 0
  TheoreticalExact = false
  Type = 0
  UnderTolerance = 0
  X = -56.8156
  Y = -76.425
FEATURE [TechDraw::DrawViewDimension] Dimension013
  Arbitrary = false
  ArbitraryTolerances = false
  EqualTolerance = true
  FormatSpec = %.2f
  FormatSpecOverTolerance = %+.2f
  FormatSpecUnderTolerance = %+.2f
  Inverted = false
  LockPosition = false
  MeasureType = 1
  OverTolerance = 0
  References2D = -> [View]
  Rotation = 0
  ScaleType = 0
  TheoreticalExact = false
  Type = 0
  UnderTolerance = 0
  X = -41.8072
  Y = -43.4209
FEATURE [TechDraw::DrawViewDimension] Dimension014
  Arbitrary = false
  ArbitraryTolerances = false
  EqualTolerance = true
  FormatSpec = %.2f
  FormatSpecOverTolerance = %+.2f
  FormatSpecUnderTolerance = %+.2f
  Inverted = false
  LockPosition = false
  MeasureType = 1
  OverTolerance = 0
  References2D = -> [View]
  Rotation = 0
  ScaleType = 0
  TheoreticalExact = false
  Type = 1
  UnderTolerance = 0
  X = 0.604255
  Y = -80.7397
FEATURE [TechDraw::DrawViewDimension] Dimension015
  Arbitrary = false
  ArbitraryTolerances = false
  EqualTolerance = true
  FormatSpec = %.2f
  FormatSpecOverTolerance = %+.2f
  FormatSpecUnderTolerance = %+.2f
  Inverted = false
  LockPosition = false
  MeasureType = 1
  OverTolerance = 0
  References2D = -> [View]
  Rotation = 0
  ScaleType = 0
  TheoreticalExact = false
  Type = 0
  UnderTolerance = 0
  X = -45.7246
  Y = -36.3292
FEATURE [TechDraw::DrawViewDimension] Dimension016
  Arbitrary = false
  ArbitraryTolerances = false
  EqualTolerance = true
  FormatSpec = %.2f
  FormatSpecOverTolerance = %+.2f
  FormatSpecUnderTolerance = %+.2f
  Inverted = false
  LockPosition = false
  MeasureType = 1
  OverTolerance = 0
  References2D = -> [View]
  Rotation = 0
  ScaleType = 0
  TheoreticalExact = false
  Type = 0
  UnderTolerance = 0
  X = 10.566
  Y = -43.8884
FEATURE [TechDraw::DrawPage] Page
  KeepUpdated = true
  NextBalloonIndex = 1
  ProjectionType = 0
  Template = -> Template
  Views = -> [View,Dimension,Dimension003,Dimension005,Dimension006,Dimension007,Dimension008,Dimension009,Dimension010,Dimension011,Dimension012,Dimension013,Dimension014,Dimension015,Dimension016]
FEATURE [App::DocumentObjectGroup] Groupe001  label="balles"
  Group = -> [Group064,Group042,Group029,Group022,Group015,Group008,Group001]
FEATURE [App::DocumentObjectGroup] Groupe  label="ModeleSACD"
  Group = -> [Group071,Groupe001]
FEATURE [PartDesign::FeatureBase] BaseFeature
  BaseFeature = -> Group071
FEATURE [Sketcher::SketchObject] Sketch
  ExternalGeometry = -> [BaseFeature]
  FullyConstrained = true
  MapMode = 5
  Placement = pos=(0,0,15) rot=(0,0,1;0rad)
  Support = -> [BaseFeature]
  sketch-geometry (12):
    g0: LineSegment StartX=-286 StartY=0 StartZ=0 EndX=-572 EndY=-495.367 EndZ=0
    g1: LineSegment StartX=-858 StartY=0 StartZ=0 EndX=-437.66 EndY=-728.05 EndZ=0
    g2: LineSegment StartX=-429 StartY=-247.683 StartZ=0 EndX=-416.01 EndY=-255.183 EndZ=0
    g3: LineSegment StartX=-429 StartY=-247.683 StartZ=0 EndX=-441.99 EndY=-240.183 EndZ=0
    g4: LineSegment StartX=-727.99 StartY=-255.183 StartZ=0 EndX=-715 EndY=-247.683 EndZ=0
    g5: LineSegment StartX=-715 StartY=-247.683 StartZ=0 EndX=-702.01 EndY=-240.183 EndZ=0
    g6: Circle CenterX=-858 CenterY=0 CenterZ=0 NormalX=0 NormalY=0 NormalZ=1 AngleXU=0 Radius=7.5
    g7: Circle CenterX=-286 CenterY=0 CenterZ=0 NormalX=0 NormalY=0 NormalZ=1 AngleXU=0 Radius=7.5
    g8: Circle CenterX=-572 CenterY=0 CenterZ=0 NormalX=0 NormalY=0 NormalZ=1 AngleXU=0 Radius=7.5
    g9: Circle CenterX=-429 CenterY=-247.683 CenterZ=0 NormalX=0 NormalY=0 NormalZ=1 AngleXU=0 Radius=7.5
    g10: Circle CenterX=-715 CenterY=-247.683 CenterZ=0 NormalX=0 NormalY=0 NormalZ=1 AngleXU=0 Radius=7.5
    g11: Circle CenterX=-572 CenterY=-495.367 CenterZ=0 NormalX=0 NormalY=0 NormalZ=1 AngleXU=0 Radius=7.5
  constraints (32):
    c: Parallel(g1,g-7)
    c: Parallel(g0,g-6)
    c: PointOnObject(g2,g-8)
    c: Coincident(g3,g2)
    c: PointOnObject(g3,g-6)
    c: Perpendicular(g2,g0)
    c: Perpendicular(g3,g0)
    c: Equal(g2,g3)
    c: PointOnObject(g0,g-1)
    c: PointOnObject(g1,g-1)
    c: PointOnObject(g4,g-7)
    c: PointOnObject(g4,g1)
    c: PointOnObject(g5,g-5)
    c: Perpendicular(g1,g4)
    c: Perpendicular(g1,g5)
    c: Equal(g4,g5)
    c: PointOnObject(g1,g-15)
    c: Symmetric(g0,g0,g2)
    c: Coincident(g4,g5)
    c: Symmetric(g0,g1,g4)
    c: Coincident(g6,g1)
    c: Coincident(g7,g0)
    c: Coincident(g10,g4)
    c: Coincident(g2,g9)
    c: Symmetric(g6,g7,g8)
    c: Coincident(g11,g0)
    c: Equal(g6,g8)
    c: Equal(g8,g7)
    c: Equal(g7,g9)
    c: Equal(g9,g10)
    c: Equal(g10,g11)
    c: Radius(g11) = 7.5
FEATURE [PartDesign::Pocket] Pocket
  BaseFeature = -> BaseFeature
  Length = 5
  Length2 = 100
  Profile = -> Sketch
  Type = 1
FEATURE [PartDesign::PolarPattern] PolarPattern
  Angle = 360
  Axis = -> Sketch [N_Axis]
  BaseFeature = -> Pocket
  Occurrences = 6
  Originals = -> [Pocket]
FEATURE [PartDesign::Body] Body
  BaseFeature = -> Group071
  Group = -> [BaseFeature,Sketch,Pocket,PolarPattern]
  Origin = -> Origin
  Tip = -> PolarPattern
FEATURE [TechDraw::DrawSVGTemplate] Template001
  Height = 210
  Orientation = 1
  Width = 297
FEATURE [TechDraw::DrawViewPart] View001
  CoarseView = false
  Direction = (0,0,1)
  Focus = 100
  HardHidden = false
  IsoCount = 0
  IsoHidden = false
  IsoVisible = false
  LockPosition = false
  Perspective = false
  Rotation = 0
  Scale = 0.1
  ScaleType = 0
  SeamHidden = false
  SeamVisible = true
  SmoothHidden = false
  SmoothVisible = true
  Source = -> [Body]
  X = 148.5
  XDirection = (1,0,0)
  Y = 105
FEATURE [TechDraw::DrawViewDimension] Dimension017
  Arbitrary = false
  ArbitraryTolerances = false
  EqualTolerance = true
  FormatSpec = %.2f
  FormatSpecOverTolerance = %+.2f
  FormatSpecUnderTolerance = %+.2f
  Inverted = false
  LockPosition = false
  MeasureType = 1
  OverTolerance = 0
  References2D = -> [View001]
  Rotation = 0
  ScaleType = 0
  TheoreticalExact = false
  Type = 0
  UnderTolerance = 0
  X = -55.9229
  Y = -74.2843
FEATURE [TechDraw::DrawViewDimension] Dimension018
  Arbitrary = false
  ArbitraryTolerances = false
  EqualTolerance = true
  FormatSpec = %.2f
  FormatSpecOverTolerance = %+.2f
  FormatSpecUnderTolerance = %+.2f
  Inverted = false
  LockPosition = false
  MeasureType = 1
  OverTolerance = 0
  References2D = -> [View001]
  Rotation = 0
  ScaleType = 0
  TheoreticalExact = false
  Type = 0
  UnderTolerance = 0
  X = -45.1273
  Y = -49.0132
FEATURE [TechDraw::DrawViewDimension] Dimension019
  Arbitrary = false
  ArbitraryTolerances = false
  EqualTolerance = true
  FormatSpec = %.2f
  FormatSpecOverTolerance = %+.2f
  FormatSpecUnderTolerance = %+.2f
  Inverted = false
  LockPosition = false
  MeasureType = 1
  OverTolerance = 0
  References2D = -> [View001]
  Rotation = 0
  ScaleType = 0
  TheoreticalExact = false
  Type = 0
  UnderTolerance = 0
  X = -33.3647
  Y = -28.4371
FEATURE [TechDraw::DrawViewDimension] Dimension020
  Arbitrary = false
  ArbitraryTolerances = false
  EqualTolerance = true
  FormatSpec = %.2f
  FormatSpecOverTolerance = %+.2f
  FormatSpecUnderTolerance = %+.2f
  Inverted = false
  LockPosition = false
  MeasureType = 1
  OverTolerance = 0
  References2D = -> [View001]
  Rotation = 0
  ScaleType = 0
  TheoreticalExact = false
  Type = 1
  UnderTolerance = 0
  X = -27.6768
  Y = -80.8511
FEATURE [TechDraw::DrawViewDimension] Dimension021
  Arbitrary = false
  ArbitraryTolerances = false
  EqualTolerance = true
  FormatSpec = %.2f
  FormatSpecOverTolerance = %+.2f
  FormatSpecUnderTolerance = %+.2f
  Inverted = false
  LockPosition = false
  MeasureType = 1
  OverTolerance = 0
  References2D = -> [View001]
  Rotation = 0
  ScaleType = 0
  TheoreticalExact = false
  Type = 1
  UnderTolerance = 0
  X = 0.419622
  Y = -80.935
FEATURE [TechDraw::DrawViewDimension] Dimension022
  Arbitrary = false
  ArbitraryTolerances = false
  EqualTolerance = true
  FormatSpec = %.2f
  FormatSpecOverTolerance = %+.2f
  FormatSpecUnderTolerance = %+.2f
  Inverted = false
  LockPosition = false
  MeasureType = 1
  OverTolerance = 0
  References2D = -> [View001]
  Rotation = 0
  ScaleType = 0
  TheoreticalExact = false
  Type = 0
  UnderTolerance = 0
  X = 5.10295
  Y = -32.7884
FEATURE [TechDraw::DrawViewDimension] Dimension023
  Arbitrary = false
  ArbitraryTolerances = false
  EqualTolerance = true
  FormatSpec = %.2f
  FormatSpecOverTolerance = %+.2f
  FormatSpecUnderTolerance = %+.2f
  Inverted = false
  LockPosition = false
  MeasureType = 1
  OverTolerance = 0
  References2D = -> [View001]
  Rotation = 0
  ScaleType = 0
  TheoreticalExact = false
  Type = 1
  UnderTolerance = 0
  X = 49.5593
  Y = -15.0234
FEATURE [TechDraw::DrawViewDimension] Dimension024
  Arbitrary = false
  ArbitraryTolerances = false
  EqualTolerance = true
  FormatSpec = %.2f
  FormatSpecOverTolerance = %+.2f
  FormatSpecUnderTolerance = %+.2f
  Inverted = false
  LockPosition = false
  MeasureType = 1
  OverTolerance = 0
  References2D = -> [View001]
  Rotation = 0
  ScaleType = 0
  TheoreticalExact = false
  Type = 1
  UnderTolerance = 0
  X = 90.0918
  Y = 19.0939
FEATURE [TechDraw::DrawViewDimension] Dimension025
  Arbitrary = false
  ArbitraryTolerances = false
  EqualTolerance = true
  FormatSpec = %.2f
  FormatSpecOverTolerance = %+.2f
  FormatSpecUnderTolerance = %+.2f
  Inverted = false
  LockPosition = false
  MeasureType = 1
  OverTolerance = 0
  References2D = -> [View001]
  Rotation = 0
  ScaleType = 0
  TheoreticalExact = false
  Type = 1
  UnderTolerance = 0
  X = 51.5482
  Y = -6.89953
FEATURE [TechDraw::DrawViewDimension] Dimension026
  Arbitrary = false
  ArbitraryTolerances = false
  EqualTolerance = true
  FormatSpec = %.2f
  FormatSpecOverTolerance = %+.2f
  FormatSpecUnderTolerance = %+.2f
  Inverted = false
  LockPosition = false
  MeasureType = 1
  OverTolerance = 0
  References2D = -> [View001]
  Rotation = 0
  ScaleType = 0
  TheoreticalExact = false
  Type = 0
  UnderTolerance = 0
  X = 28.914
  Y = 29.8209
FEATURE [TechDraw::DrawViewDimension] Dimension027
  Arbitrary = false
  ArbitraryTolerances = false
  EqualTolerance = true
  FormatSpec = %.2f
  FormatSpecOverTolerance = %+.2f
  FormatSpecUnderTolerance = %+.2f
  Inverted = false
  LockPosition = false
  MeasureType = 1
  OverTolerance = 0
  References2D = -> [View001]
  Rotation = 0
  ScaleType = 0
  TheoreticalExact = false
  Type = 0
  UnderTolerance = 0
  X = 92.5988
  Y = 50.9544
FEATURE [TechDraw::DrawViewDimension] Dimension029
  Arbitrary = false
  ArbitraryTolerances = false
  EqualTolerance = true
  FormatSpec = %.2f
  FormatSpecOverTolerance = %+.2f
  FormatSpecUnderTolerance = %+.2f
  Inverted = false
  LockPosition = false
  MeasureType = 1
  OverTolerance = 0
  References2D = -> [View001]
  Rotation = 0
  ScaleType = 0
  TheoreticalExact = false
  Type = 0
  UnderTolerance = 0
  X = 64.7014
  Y = 20.8848
FEATURE [TechDraw::DrawViewDimension] Dimension030
  Arbitrary = false
  ArbitraryTolerances = false
  EqualTolerance = true
  FormatSpec = %.2f
  FormatSpecOverTolerance = %+.2f
  FormatSpecUnderTolerance = %+.2f
  Inverted = false
  LockPosition = false
  MeasureType = 1
  OverTolerance = 0
  References2D = -> [View001]
  Rotation = 0
  ScaleType = 0
  TheoreticalExact = false
  Type = 6
  UnderTolerance = 0
  X = 51.2161
  Y = 15.5467
FEATURE [TechDraw::DrawPage] Page001
  KeepUpdated = true
  NextBalloonIndex = 1
  ProjectionType = 0
  Template = -> Template001
  Views = -> [View001,Dimension017,Dimension018,Dimension019,Dimension020,Dimension021,Dimension022,Dimension023,Dimension024,Dimension025,Dimension026,Dimension027,Dimension029,Dimension030]
